# Revit family: Напольно-потолочный блок VRF системы
name_source: partatom
category: Оборудование
revit_build: Autodesk Revit 2016 (Build: 20150714_1515(x64)
units: mm (PartAtom-declared; Revit-internal decimal feet)

## family parameters
Общий = Нет
Основа = Грань
При загрузке вырезать с полостями = Нет
Размер круглого соединителя = Использовать диаметр
Тип детали = Нормальный
Точка расчета площади = Нет

## types (5) — shared parameters
Высота = 680 мм
Глубина = 230 мм
Диаметр газовой трубы = 15.88 мм
Наименование = Напольно-потолочный блок VRF-системы
Номинал предохранителя = 10 А
Отметка по умолчанию = 1219.2 мм
Производитель = Electrolux
Таблица модель = Модель
Таблица наименование = Наименование
Таблица параметров = Таблица параметров
Таблица расход воздуха = Расход воздуха
Таблица уровень звукового давления = Уровень звукового давления
Таблица электропитание = Электропитание
Фаза = 1
Частота сети = 50 Гц
Эл. питание(коннектор) = 220 В
Электропитание, (В) = 220

## per-type parameters (varying)
| type | Артикул | Вес | Диаметр жидкостной трубы | Длина сопла | Максимальная потребляемая мощность | Расход воздуха, (м.куб/ч) | Теплопроизводительность | Уровень звукового давления, (Дб(А)) | Холодопроизводительность | Ширина |
| ESVMU-SF-56 | 1040302 | 31.00 кг | 6.35 мм | 890 мм | 0.08 кВт | 780-600-540 | 6.50 кВт | 35-33-29 | 5.60 кВт | 990 мм |
| ESVMU-SF-71 | 1022714 | 34.00 кг | 9.53 мм | 890 мм | 0.11 кВт | 966-840-687 | 8.50 кВт | 40-38-35 | 7.10 кВт | 990 мм |
| ESVMU-SF-90 | 1022715 | 44.00 кг | 9.53 мм | 1185 мм | 0.16 кВт | 1176-978-798 | 10.00 кВт | 42-39-36 | 9.00 кВт | 1285 мм |
| ESVMU-SF-112 | 1022716 | 45.00 кг | 9.53 мм | 1185 мм | 0.20 кВт | 1488-1230-978 | 13.00 кВт | 46-42-38 | 11.20 кВт | 1285 мм |
| ESVMU-SF-140 | 1022717 | 47.00 кг | 9.53 мм | 1480 мм | 0.27 кВт | 1980-1680-1380 | 16.30 кВт | 46-43-39 | 14.20 кВт | 1580 мм |

note: column(s) folded — value = type name in every type: Модель
